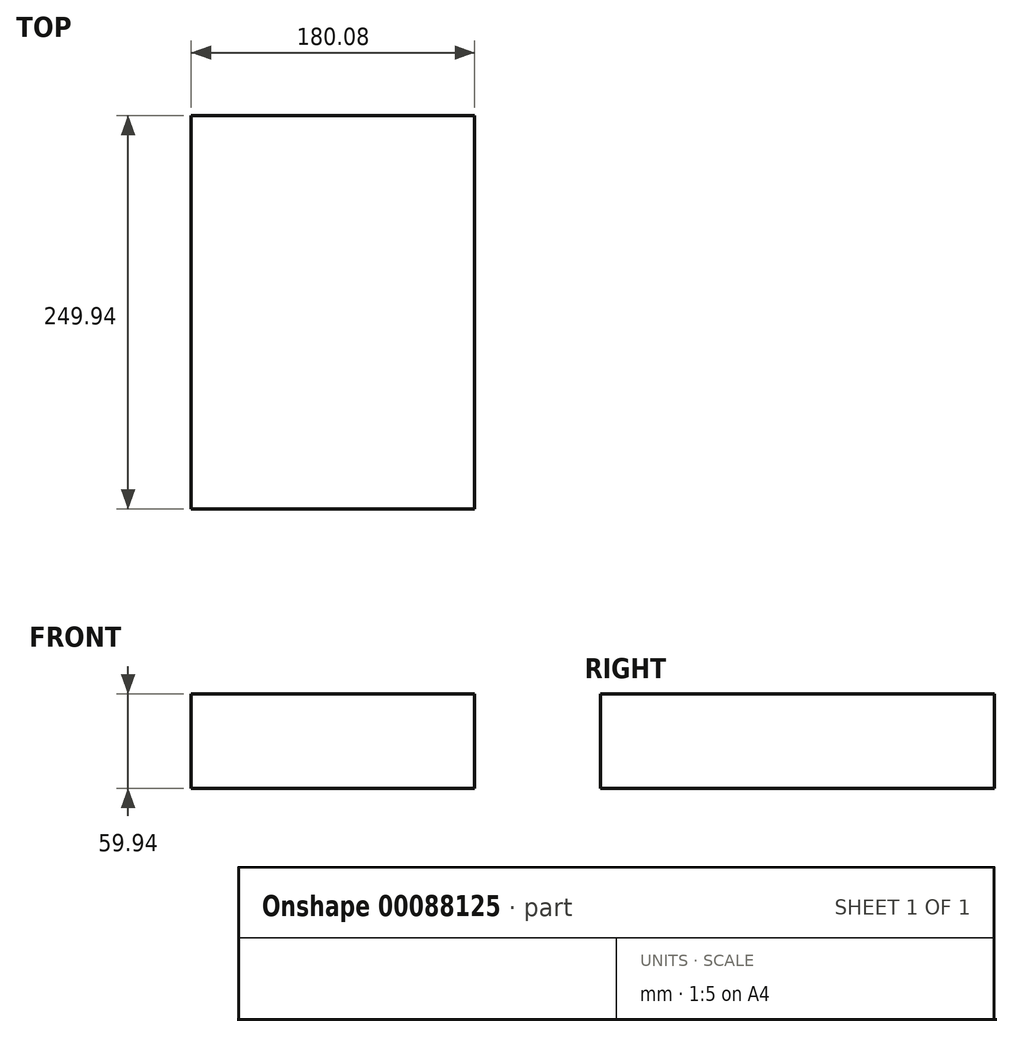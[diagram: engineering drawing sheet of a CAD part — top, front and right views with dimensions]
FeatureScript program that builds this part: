
annotation { "Feature Type Name" : "Feature", "Feature Type Description" : "" }
export const myFeature = defineFeature(function(context is Context, id is Id, definition is map)
    precondition{}
    {
        {
            var Q0;
            Q0=qCreatedBy(makeId("Top.planeOp"),FACE);
            var sketch = newSketch(context, id + "F0", { "sketchPlane" : qUnion([Q0])});
            skLineSegment(sketch, "E0.bottom", {"start": v(90.04, -124.97) * mm, "end": v(-90.04, -124.97) * mm});
            skLineSegment(sketch, "E0.top", {"start": v(90.04, 124.97) * mm, "end": v(-90.04, 124.97) * mm});
            skLineSegment(sketch, "E0.left", {"start": v(90.04, -124.97) * mm, "end": v(90.04, 124.97) * mm});
            skLineSegment(sketch, "E0.right", {"start": v(-90.04, -124.97) * mm, "end": v(-90.04, 124.97) * mm});
            skPoint(sketch, "E0.middle", {"position": v(0, 0) * mm});
            skSolve(sketch);
        }
        {
            var Q0;
            Q0=makeQuery(id+"F0.imprint","IMPRINT",FACE,{"disambiguationData":[TD([[makeQuery(id+"F0.imprint","IMPRINT",EDGE,{"derivedFrom":sQuery(id+"F0.wireOp",EDGE,"E0.bottom")}),-1.0]])]});
            extrude(context, id + "F1", {"entities" : qUnion([Q0]), "depth" : 59.94 * mm});
        }
    });
